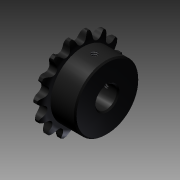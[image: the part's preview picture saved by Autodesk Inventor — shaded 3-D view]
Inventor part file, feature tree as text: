
AUTODESK INVENTOR PART (.ipt)
format: ipt  version: 2011 (Build 150239000, 239)  size: 382,464 bytes
history: native  units: mm
features: other x6, extrude x4, sketch x4, pattern_circular x2, hole x2, chamfer x2, pattern_linear x1, plane x1
ambient origin geometry x8: Origin, YZ Plane, XZ Plane, XY Plane, X Axis, Y Axis, Z Axis, Center Point
bodies: Solid1 (feature_tree)
feature tree (22):
  other  "Theoretical Tooth Profile"
  other  "Tooth Profile"
  other  "Section Profile"
  other  "Shroud"
  other  "Strand"
  pattern_linear  "Strand Pattern"  Spacing1=2.490003mm  [1 undecoded]
  extrude  "Theoretical Tooth"  Depth=4.064mm
  extrude  "Tooth"  Depth=6.6548mm
  pattern_circular  "Tooth Pattern"  [2 undecoded]
  other  "Timing Plane"
  extrude  "Extrusion4"  Depth=10.0mm TaperAngle=0.0deg
  hole  "Hole1"  [1 undecoded]
  extrude  "Extrusion5"  TaperAngle=360.0deg  [1 undecoded]
  chamfer  "Chamfer1"  Distance=2.8575mm
  chamfer  "Chamfer2"  [1 undecoded]
  plane  "Work Plane3"
  hole  "Hole2"  [1 undecoded]
  pattern_circular  "Circular Pattern2"  [2 undecoded]
  sketch  "Sketch4"  dims[d0=45.81272mm]
  sketch  "Sketch5"  dims[d2=4.18879mm]
  sketch  "Sketch6"  dims[d3=2.5908mm]
  sketch  "Sketch7"  dims[d10=22.514747mm d11=2.490003mm d12=4.064mm d13=6.6548mm d14=7.112mm d18=10.0mm d19=0.0mm d20=150.0mm d21=360.0deg d23=2.8575mm d28=0.0mm d29=0.0mm d30=4.593336mm d31=33.762602mm d32=4.593336mm d33=1.190625mm d34=10.125075mm d36=90.0deg d37=90.0deg d38=10.0mm d40=10.1346mm d42=0.0mm d43=2.296668mm d44=23.387412mm d45=2.5908mm d46=10.3632mm d47=0.0mm d48=25.4mm d49=0.0mm d50=10.0mm d51=38.1mm d52=14.53134mm d53=0.0mm d54=12.7mm d55=12.7mm d56=9.525mm d57=6.35mm d58=14.3117mm d59=19.05mm d60=20.594885mm d61=3.175mm d62=1.524mm d63=19.05mm d64=0.0mm d65=0.79375mm d66=3.175mm d67=45.0deg d68=0.79375mm d69=3.175mm d70=45.0deg d71=7.540625mm d72=3.683mm d73=12.7mm d74=9.525mm d75=6.35mm d76=14.3117mm d77=19.05mm d78=20.594885mm d79=20.0mm d80=-15.707963mm]
note: 9 required parameter values undecoded (feature->parameter linkage not recoverable at this tier; creation-order binding heuristic only, values carry confidence <= 0.55)
